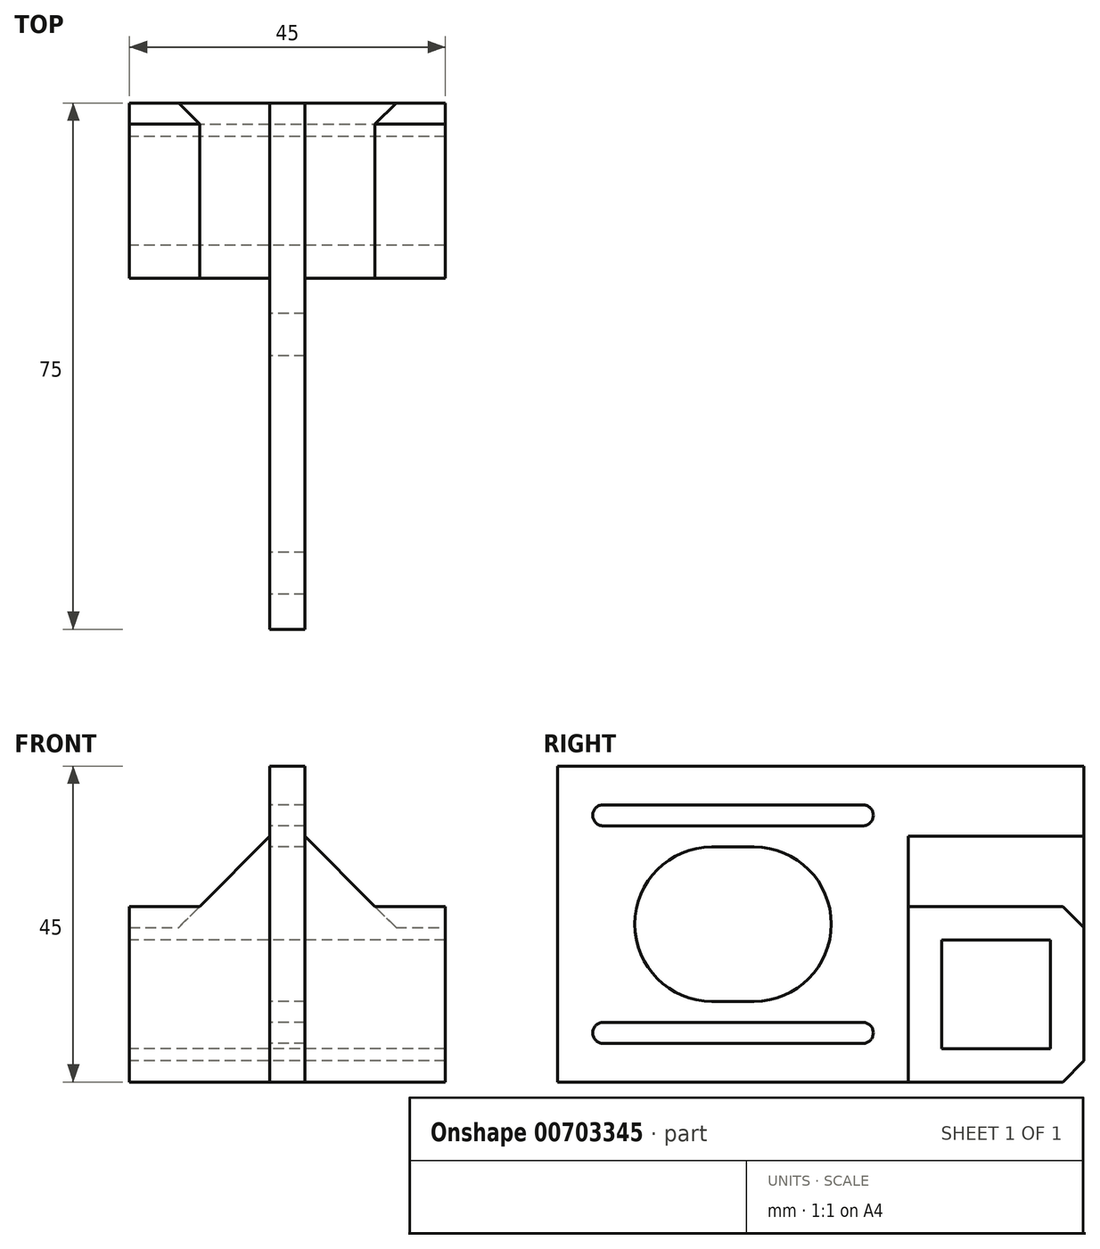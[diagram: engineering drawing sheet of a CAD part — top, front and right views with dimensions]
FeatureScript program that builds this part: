
annotation { "Feature Type Name" : "Feature", "Feature Type Description" : "" }
export const myFeature = defineFeature(function(context is Context, id is Id, definition is map)
    precondition{}
    {
        {
            var Q0;
            Q0=qCreatedBy(makeId("Right.planeOp"),FACE);
            var sketch = newSketch(context, id + "F0", { "sketchPlane" : qUnion([Q0])});
            skLineSegment(sketch, "E0.bottom", {"start": v(-19.76, 10.69) * mm, "end": v(-35.26, 10.69) * mm});
            skLineSegment(sketch, "E0.top", {"start": v(-19.76, 26.19) * mm, "end": v(-35.26, 26.19) * mm});
            skLineSegment(sketch, "E0.left", {"start": v(-19.76, 10.69) * mm, "end": v(-19.76, 26.19) * mm});
            skLineSegment(sketch, "E0.right", {"start": v(-35.26, 10.69) * mm, "end": v(-35.26, 26.19) * mm});
            skPoint(sketch, "E0.middle", {"position": v(-27.51, 18.44) * mm});
            skLineSegment(sketch, "E1.bottom", {"start": v(-40.01, 30.94) * mm, "end": v(-15.01, 30.94) * mm});
            skLineSegment(sketch, "E1.top", {"start": v(-40.01, 5.94) * mm, "end": v(-15.01, 5.94) * mm});
            skLineSegment(sketch, "E1.left", {"start": v(-40.01, 30.94) * mm, "end": v(-40.01, 5.94) * mm});
            skLineSegment(sketch, "E1.right", {"start": v(-15.01, 30.94) * mm, "end": v(-15.01, 5.94) * mm});
            skLineSegment(sketch, "E2", {"start": v(-40.01, 5.94) * mm, "end": v(-90.01, 5.94) * mm});
            skLineSegment(sketch, "E3", {"start": v(-90.01, 5.94) * mm, "end": v(-90.01, 50.94) * mm});
            skLineSegment(sketch, "E4", {"start": v(-90.01, 50.94) * mm, "end": v(-40.01, 50.94) * mm});
            skLineSegment(sketch, "E5.bottom", {"start": v(-87.51, 48.69) * mm, "end": v(-42.51, 48.69) * mm, "construction": true});
            skLineSegment(sketch, "E5.top", {"start": v(-87.51, 6.69) * mm, "end": v(-42.51, 6.69) * mm, "construction": true});
            skLineSegment(sketch, "E5.left", {"start": v(-87.51, 48.69) * mm, "end": v(-87.51, 6.69) * mm, "construction": true});
            skLineSegment(sketch, "E5.right", {"start": v(-42.51, 48.69) * mm, "end": v(-42.51, 6.69) * mm, "construction": true});
            skLineSegment(sketch, "E6", {"start": v(-40.01, 50.94) * mm, "end": v(-90.01, 5.94) * mm, "construction": true});
            skLineSegment(sketch, "E7", {"start": v(-90.01, 50.94) * mm, "end": v(-40.01, 5.94) * mm, "construction": true});
            skCircle(sketch, "E8", {"center": v(-62.01, 28.44) * mm, "radius": 11 * mm});
            skLineSegment(sketch, "E9.bottom", {"start": v(-83.51, 43.94) * mm, "end": v(-46.51, 43.94) * mm, "construction": true});
            skLineSegment(sketch, "E9.top", {"start": v(-83.51, 12.94) * mm, "end": v(-46.51, 12.94) * mm, "construction": true});
            skLineSegment(sketch, "E9.left", {"start": v(-83.51, 43.94) * mm, "end": v(-83.51, 12.94) * mm, "construction": true});
            skLineSegment(sketch, "E9.right", {"start": v(-46.51, 43.94) * mm, "end": v(-46.51, 12.94) * mm, "construction": true});
            skPoint(sketch, "E9.middle", {"position": v(-65.01, 28.44) * mm});
            skCircle(sketch, "E10", {"center": v(-83.51, 43.94) * mm, "radius": 1.5 * mm});
            skCircle(sketch, "E11", {"center": v(-46.51, 43.94) * mm, "radius": 1.5 * mm});
            skCircle(sketch, "E12", {"center": v(-46.51, 12.94) * mm, "radius": 1.5 * mm});
            skCircle(sketch, "E13", {"center": v(-83.51, 12.94) * mm, "radius": 1.5 * mm});
            skLineSegment(sketch, "E14", {"start": v(-83.51, 42.44) * mm, "end": v(-46.51, 42.44) * mm});
            skLineSegment(sketch, "E15", {"start": v(-46.51, 42.44) * mm, "end": v(-46.51, 45.44) * mm});
            skLineSegment(sketch, "E16", {"start": v(-46.51, 45.44) * mm, "end": v(-83.51, 45.44) * mm});
            skLineSegment(sketch, "E17", {"start": v(-83.51, 14.44) * mm, "end": v(-46.51, 14.44) * mm});
            skLineSegment(sketch, "E18", {"start": v(-46.51, 14.44) * mm, "end": v(-46.51, 11.44) * mm});
            skLineSegment(sketch, "E19", {"start": v(-46.51, 11.44) * mm, "end": v(-83.51, 11.44) * mm});
            skLineSegment(sketch, "E20", {"start": v(-15.01, 30.94) * mm, "end": v(-15.01, 50.94) * mm});
            skLineSegment(sketch, "E21", {"start": v(-15.01, 50.94) * mm, "end": v(-40.01, 50.94) * mm});
            skLineSegment(sketch, "E22", {"start": v(-46.51, 28.44) * mm, "end": v(-83.51, 28.44) * mm, "construction": true});
            skCircle(sketch, "E23", {"center": v(-68.01, 28.44) * mm, "radius": 11 * mm});
            skLineSegment(sketch, "E24", {"start": v(-65.01, 43.94) * mm, "end": v(-65.01, 12.94) * mm, "construction": true});
            skLineSegment(sketch, "E25", {"start": v(-62.01, 39.44) * mm, "end": v(-68.01, 39.44) * mm});
            skLineSegment(sketch, "E26", {"start": v(-62.01, 17.44) * mm, "end": v(-68.01, 17.44) * mm});
            skSolve(sketch);
        }
        {
            var Q0;
            Q0 = qSketchRegion(id + "F0", true);
            extrude(context, id + "F1", {"entities" : qUnion([Q0]), "depth" : 5 * mm, "offsetDistance" : 25 * mm});
        }
        {
            var Q0;
            Q0=makeQuery(id+"F0.imprint","IMPRINT",FACE,{"disambiguationData":[TD([[makeQuery(id+"F0.imprint","IMPRINT",EDGE,{"derivedFrom":sQuery(id+"F0.wireOp",EDGE,"E0.bottom")}),1.0]])]});
            extrude(context, id + "F2", {"entities" : qUnion([Q0]), "operationType" : NewBodyOperationType.ADD, "depth" : 25 * mm, "offsetDistance" : 25 * mm, "hasSecondDirection" : true, "secondDirectionOppositeDirection" : true, "secondDirectionDepth" : 20 * mm});
        }
        {
            var Q0;
            Q0=makeQuery(id+"F2.boolean.opBoolean","INTERSECT",EDGE,{"derivedFrom":[makeQuery(id+"F1.opExtrude","CAP_FACE",FACE,{"disambiguationData":[OSD([sQuery(id+"F0.wireOp",EDGE,"E0.bottom"),sQuery(id+"F0.wireOp",EDGE,"E0.top"),sQuery(id+"F0.wireOp",EDGE,"E0.left"),sQuery(id+"F0.wireOp",EDGE,"E0.right"),sQuery(id+"F0.wireOp",EDGE,"E1.top"),sQuery(id+"F0.wireOp",EDGE,"E1.right"),sQuery(id+"F0.wireOp",EDGE,"E2"),sQuery(id+"F0.wireOp",EDGE,"E3"),sQuery(id+"F0.wireOp",EDGE,"E4"),sQuery(id+"F0.wireOp",EDGE,"XVBOKlDE-7pjN-uC1c-cPKv-9xq2yWt4VhJJ"),sQuery(id+"F0.wireOp",EDGE,"E8"),sQuery(id+"F0.wireOp",EDGE,"FD3xqKPC-oB8C-ilbH-hPQw-PRNj99xJCRT6"),sQuery(id+"F0.wireOp",EDGE,"kwXWCx0E-mGV2-ynGZ-OXdg-stRwIDYBOgCq"),sQuery(id+"F0.wireOp",EDGE,"1pxGhbmu-zXL3-4LJ0-MEkR-QQfTb31C06Ag"),sQuery(id+"F0.wireOp",EDGE,"L5ztBN08-ZWqF-sM5d-UjDZ-yCwkQc2p9zZG")])],"isStart":false}),makeQuery(id+"F2.opExtrude","SWEPT_FACE",FACE,{"disambiguationData":[OSD([sQuery(id+"F0.wireOp",EDGE,"E1.bottom")])]})]});
            var Q1;
            Q1=makeQuery(id+"F2.boolean.opBoolean","INTERSECT",EDGE,{"derivedFrom":[makeQuery(id+"F1.opExtrude","CAP_FACE",FACE,{"disambiguationData":[OSD([sQuery(id+"F0.wireOp",EDGE,"E0.bottom"),sQuery(id+"F0.wireOp",EDGE,"E0.top"),sQuery(id+"F0.wireOp",EDGE,"E0.left"),sQuery(id+"F0.wireOp",EDGE,"E0.right"),sQuery(id+"F0.wireOp",EDGE,"E1.top"),sQuery(id+"F0.wireOp",EDGE,"E1.right"),sQuery(id+"F0.wireOp",EDGE,"E2"),sQuery(id+"F0.wireOp",EDGE,"E3"),sQuery(id+"F0.wireOp",EDGE,"E4"),sQuery(id+"F0.wireOp",EDGE,"XVBOKlDE-7pjN-uC1c-cPKv-9xq2yWt4VhJJ"),sQuery(id+"F0.wireOp",EDGE,"E8"),sQuery(id+"F0.wireOp",EDGE,"FD3xqKPC-oB8C-ilbH-hPQw-PRNj99xJCRT6"),sQuery(id+"F0.wireOp",EDGE,"kwXWCx0E-mGV2-ynGZ-OXdg-stRwIDYBOgCq"),sQuery(id+"F0.wireOp",EDGE,"1pxGhbmu-zXL3-4LJ0-MEkR-QQfTb31C06Ag"),sQuery(id+"F0.wireOp",EDGE,"L5ztBN08-ZWqF-sM5d-UjDZ-yCwkQc2p9zZG")])],"isStart":true}),makeQuery(id+"F2.opExtrude","SWEPT_FACE",FACE,{"disambiguationData":[OSD([sQuery(id+"F0.wireOp",EDGE,"E1.bottom")])]})]});
            chamfer(context, id + "F3", {"entities" : qUnion([Q0, Q1]), "width" : 10 * mm, "tangentPropagation" : true});
        }
        {
            var Q0;
            {var subQ0=sQuery(id+"F0.wireOp",EDGE,"E1.right");var subQ1=sQuery(id+"F0.wireOp",EDGE,"E1.top");Q0=makeQuery(id+"F2.boolean.opBoolean","MERGE",EDGE,{"derivedFrom":[makeQuery(id+"F1.opExtrude","SWEPT_EDGE",EDGE,{"disambiguationData":[OSD([subQ1,subQ0])]}),makeQuery(id+"F2.opExtrude","SWEPT_EDGE",EDGE,{"disambiguationData":[OSD([subQ1,subQ0])]})]});}
            var Q1;
            {var subQ0=sQuery(id+"F0.wireOp",EDGE,"E1.right");var subQ1=sQuery(id+"F0.wireOp",EDGE,"E1.top");var subQ2=sQuery(id+"F0.wireOp",EDGE,"E1.bottom");var subQ3=sQuery(id+"F0.wireOp",EDGE,"E0.right");var subQ4=sQuery(id+"F0.wireOp",EDGE,"E0.left");var subQ5=sQuery(id+"F0.wireOp",EDGE,"E0.top");var subQ6=sQuery(id+"F0.wireOp",EDGE,"E0.bottom");var subQ7=sQuery(id+"F0.wireOp",EDGE,"XVBOKlDE-7pjN-uC1c-cPKv-9xq2yWt4VhJJ");Q1=makeQuery(id+"F2.boolean.opBoolean","SPLIT",EDGE,{"disambiguationData":[TD([makeQuery(id+"F2.opExtrude","CAP_FACE",FACE,{"disambiguationData":[OSD([subQ6,subQ5,subQ4,subQ3,subQ2,subQ1,sQuery(id+"F0.wireOp",EDGE,"E1.left"),subQ0])],"isStart":false})])],"derivedFrom":makeQuery(id+"F2.opExtrude","SWEPT_EDGE",EDGE,{"disambiguationData":[OSD([subQ2,subQ0,subQ7])]})});}
            var Q2;
            {var subQ0=sQuery(id+"F0.wireOp",EDGE,"XVBOKlDE-7pjN-uC1c-cPKv-9xq2yWt4VhJJ");var subQ1=sQuery(id+"F0.wireOp",EDGE,"E1.bottom");var subQ2=sQuery(id+"F0.wireOp",EDGE,"E1.right");var subQ3=sQuery(id+"F0.wireOp",EDGE,"E1.top");var subQ4=sQuery(id+"F0.wireOp",EDGE,"E0.right");var subQ5=sQuery(id+"F0.wireOp",EDGE,"E0.left");var subQ6=sQuery(id+"F0.wireOp",EDGE,"E0.top");var subQ7=sQuery(id+"F0.wireOp",EDGE,"E0.bottom");Q2=makeQuery(id+"F2.boolean.opBoolean","SPLIT",EDGE,{"disambiguationData":[TD([makeQuery(id+"F2.opExtrude","CAP_FACE",FACE,{"disambiguationData":[OSD([subQ7,subQ6,subQ5,subQ4,subQ1,subQ3,sQuery(id+"F0.wireOp",EDGE,"E1.left"),subQ2])],"isStart":true})])],"derivedFrom":makeQuery(id+"F2.opExtrude","SWEPT_EDGE",EDGE,{"disambiguationData":[OSD([subQ1,subQ2,subQ0])]})});}
            chamfer(context, id + "F4", {"entities" : qUnion([Q0, Q1, Q2]), "width" : 3 * mm, "tangentPropagation" : true});
        }
    });
